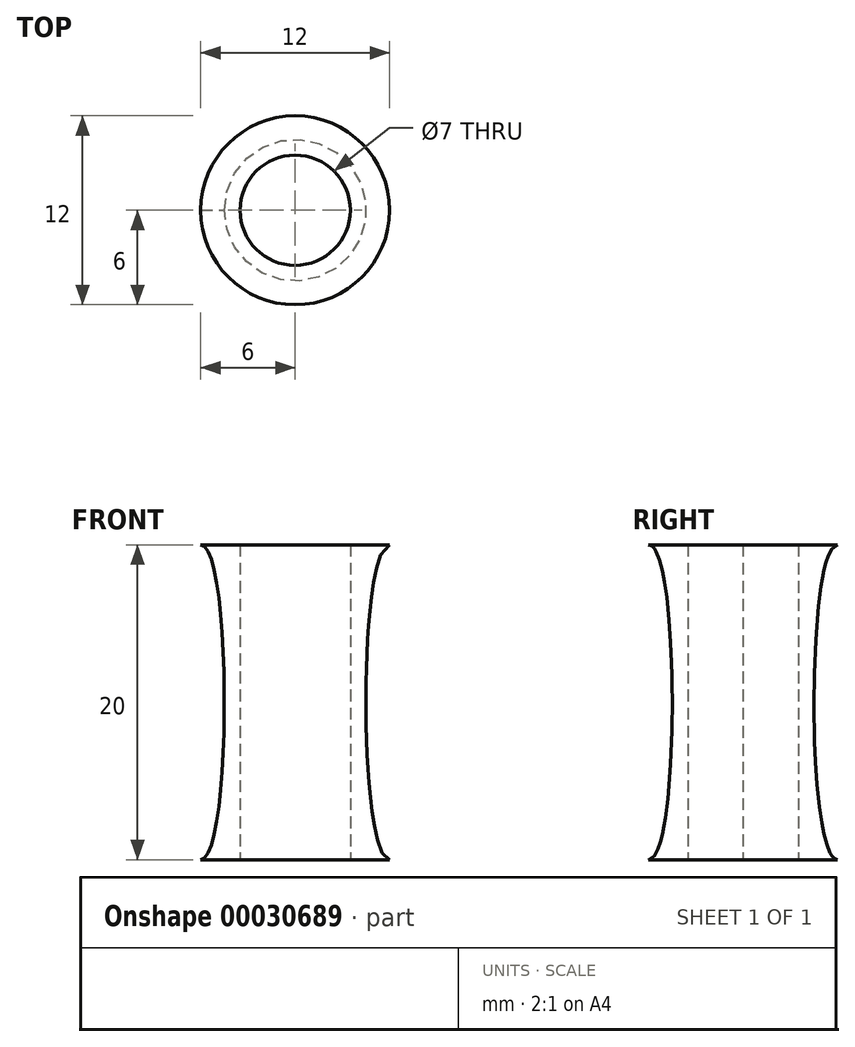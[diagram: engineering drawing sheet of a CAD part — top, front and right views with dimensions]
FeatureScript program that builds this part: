
annotation { "Feature Type Name" : "Feature", "Feature Type Description" : "" }
export const myFeature = defineFeature(function(context is Context, id is Id, definition is map)
    precondition{}
    {
        {
            var Q0;
            Q0=qCreatedBy(makeId("Front.planeOp"),FACE);
            var sketch = newSketch(context, id + "F0", { "sketchPlane" : qUnion([Q0])});
            skLineSegment(sketch, "E0.bottom", {"start": v(3.5, 0) * mm, "end": v(6, 0) * mm});
            skLineSegment(sketch, "E0.top", {"start": v(3.5, 20) * mm, "end": v(6, 20) * mm});
            skLineSegment(sketch, "E0.left", {"start": v(3.5, 0) * mm, "end": v(3.5, 20) * mm});
            skLineSegment(sketch, "E1", {"start": v(0, 0) * mm, "end": v(0, 21.2) * mm, "construction": true});
            skFitSpline(sketch, "E2", {"points": [v(6, 20) * mm, v(6, 0) * mm], "startDerivative": vector(-6, 0) * mm, "endDerivative": vector(6, 0) * mm});
            skLineSegment(sketch, "E3", {"start": v(4, 20) * mm, "end": v(3.5, 20) * mm, "construction": true});
            skLineSegment(sketch, "E4", {"start": v(4, 0) * mm, "end": v(4, 20) * mm, "construction": true});
            skLineSegment(sketch, "E5", {"start": v(4.5, 20) * mm, "end": v(4.5, 0) * mm, "construction": true});
            skSolve(sketch);
        }
        {
            var Q0;
            Q0=makeQuery(id+"F0.imprint","IMPRINT",FACE,{"disambiguationData":[TD([[makeQuery(id+"F0.imprint","IMPRINT",EDGE,{"derivedFrom":sQuery(id+"F0.wireOp",EDGE,"E0.bottom")}),1.0]])]});
            var Q1;
            Q1=sQuery(id+"F0.wireOp",EDGE,"E1");
            revolve(context, id + "F1", {"entities" : qUnion([Q0]), "axis" : qUnion([Q1]), "revolveType" : RevolveType.FULL});
        }
    });
